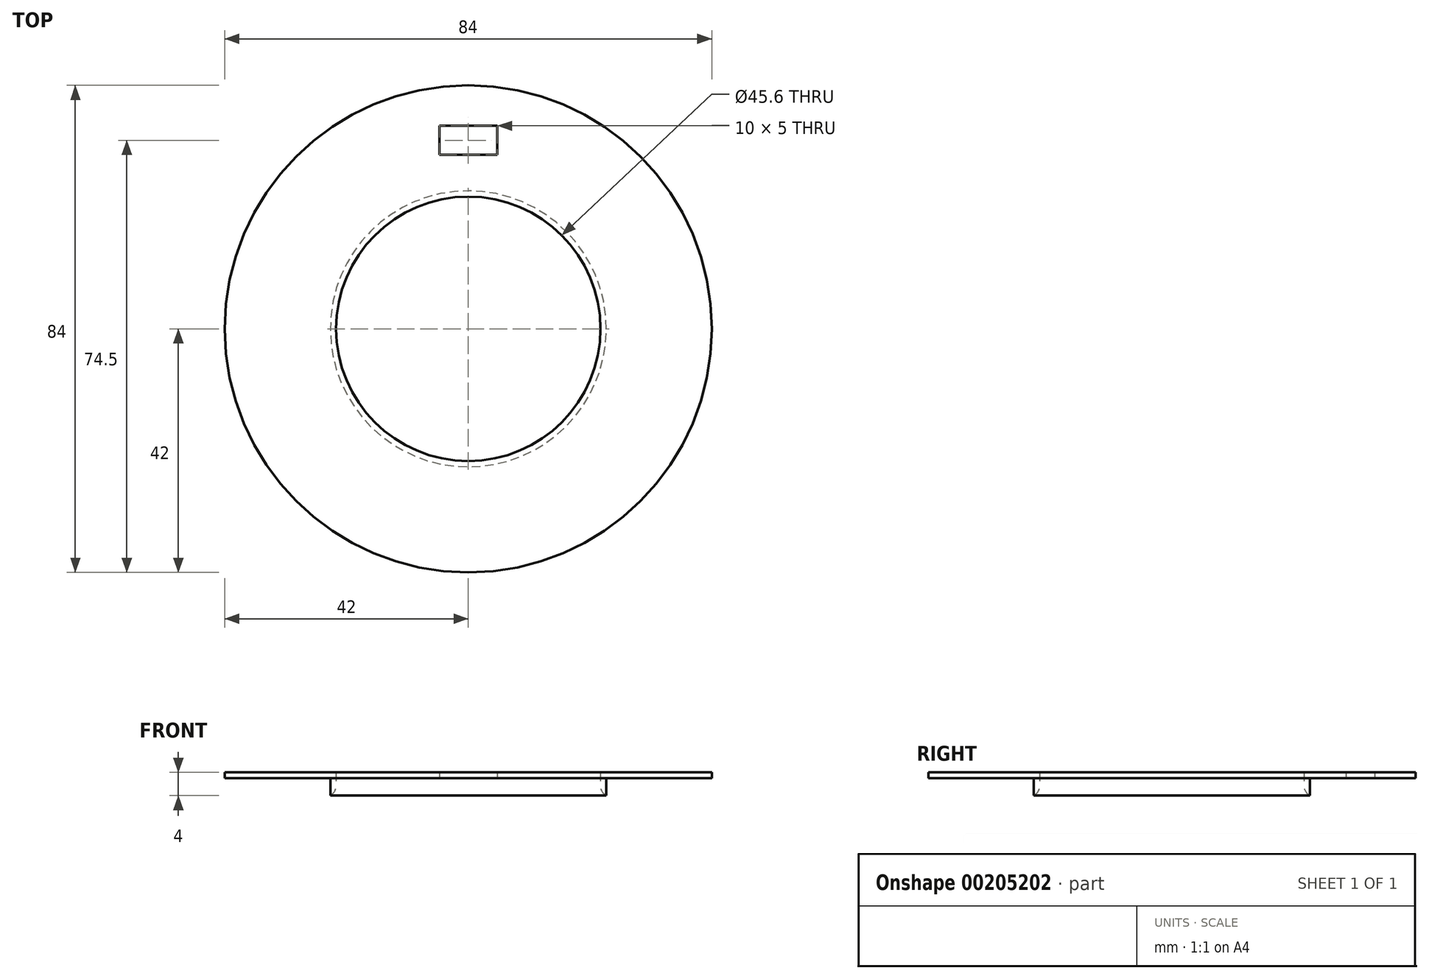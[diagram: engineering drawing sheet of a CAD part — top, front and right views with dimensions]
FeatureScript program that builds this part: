
annotation { "Feature Type Name" : "Feature", "Feature Type Description" : "" }
export const myFeature = defineFeature(function(context is Context, id is Id, definition is map)
    precondition{}
    {
        {
            var Q0;
            Q0=qCreatedBy(makeId("Front.planeOp"),FACE);
            var sketch = newSketch(context, id + "F0", { "sketchPlane" : qUnion([Q0])});
            skLineSegment(sketch, "E0", {"start": v(0, 0) * mm, "end": v(0, 0) * mm});
            skLineSegment(sketch, "E1", {"start": v(23.8, -3) * mm, "end": v(23.8, 0) * mm});
            skLineSegment(sketch, "E2", {"start": v(23.8, 0) * mm, "end": v(42, 0) * mm});
            skLineSegment(sketch, "E3.0", {"start": v(22.8, 1) * mm, "end": v(42, 1) * mm});
            skLineSegment(sketch, "E4.0", {"start": v(22.8, -3) * mm, "end": v(22.8, 1) * mm});
            skLineSegment(sketch, "E5", {"start": v(22.8, -3) * mm, "end": v(23.8, -3) * mm});
            skLineSegment(sketch, "E6", {"start": v(42, 1) * mm, "end": v(42, 0) * mm});
            skLineSegment(sketch, "E7", {"start": v(0, 0) * mm, "end": v(0, 8.03) * mm, "construction": true});
            skSolve(sketch);
        }
        {
            var Q0;
            Q0=makeQuery(id+"F0.imprint","IMPRINT",FACE,{"disambiguationData":[TD([[makeQuery(id+"F0.imprint","IMPRINT",EDGE,{"derivedFrom":sQuery(id+"F0.wireOp",EDGE,"E1")}),1.0]])]});
            var Q1;
            Q1=sQuery(id+"F0.wireOp",EDGE,"E7");
            revolve(context, id + "F1", {"entities" : qUnion([Q0]), "axis" : qUnion([Q1]), "revolveType" : RevolveType.FULL});
        }
        {
            var Q0;
            Q0=qCreatedBy(makeId("Top.planeOp"),FACE);
            var sketch = newSketch(context, id + "F2", { "sketchPlane" : qUnion([Q0])});
            skLineSegment(sketch, "E8", {"start": v(0, 0) * mm, "end": v(0, 30) * mm, "construction": true});
            skLineSegment(sketch, "E9", {"start": v(0, 30) * mm, "end": v(-5, 30) * mm});
            skLineSegment(sketch, "E10", {"start": v(-5, 30) * mm, "end": v(-5, 35) * mm});
            skLineSegment(sketch, "E11", {"start": v(-5, 35) * mm, "end": v(5, 35) * mm});
            skLineSegment(sketch, "E12", {"start": v(5, 35) * mm, "end": v(5, 30) * mm});
            skLineSegment(sketch, "E13", {"start": v(5, 30) * mm, "end": v(0, 30) * mm});
            skSolve(sketch);
        }
        {
            var Q0;
            Q0=makeQuery(id+"F2.imprint","IMPRINT",FACE,{"disambiguationData":[TD([[makeQuery(id+"F2.imprint","IMPRINT",EDGE,{"derivedFrom":sQuery(id+"F2.wireOp",EDGE,"E9")}),-1.0]])]});
            extrude(context, id + "F3", {"entities" : qUnion([Q0]), "operationType" : NewBodyOperationType.REMOVE, "depth" : 25 * mm});
        }
        {
            var Q0;
            Q0=makeQuery(id+"F1.opRevolve","SWEPT_EDGE",EDGE,{"disambiguationData":[OSD([sQuery(id+"F0.wireOp",EDGE,"E4.0"),sQuery(id+"F0.wireOp",EDGE,"E5")])]});
            fillet(context, id + "F4", {"entities" : qUnion([Q0]), "radius" : 2 * mm, "tangentPropagation" : true, "allowEdgeOverflow" : false});
        }
    });
